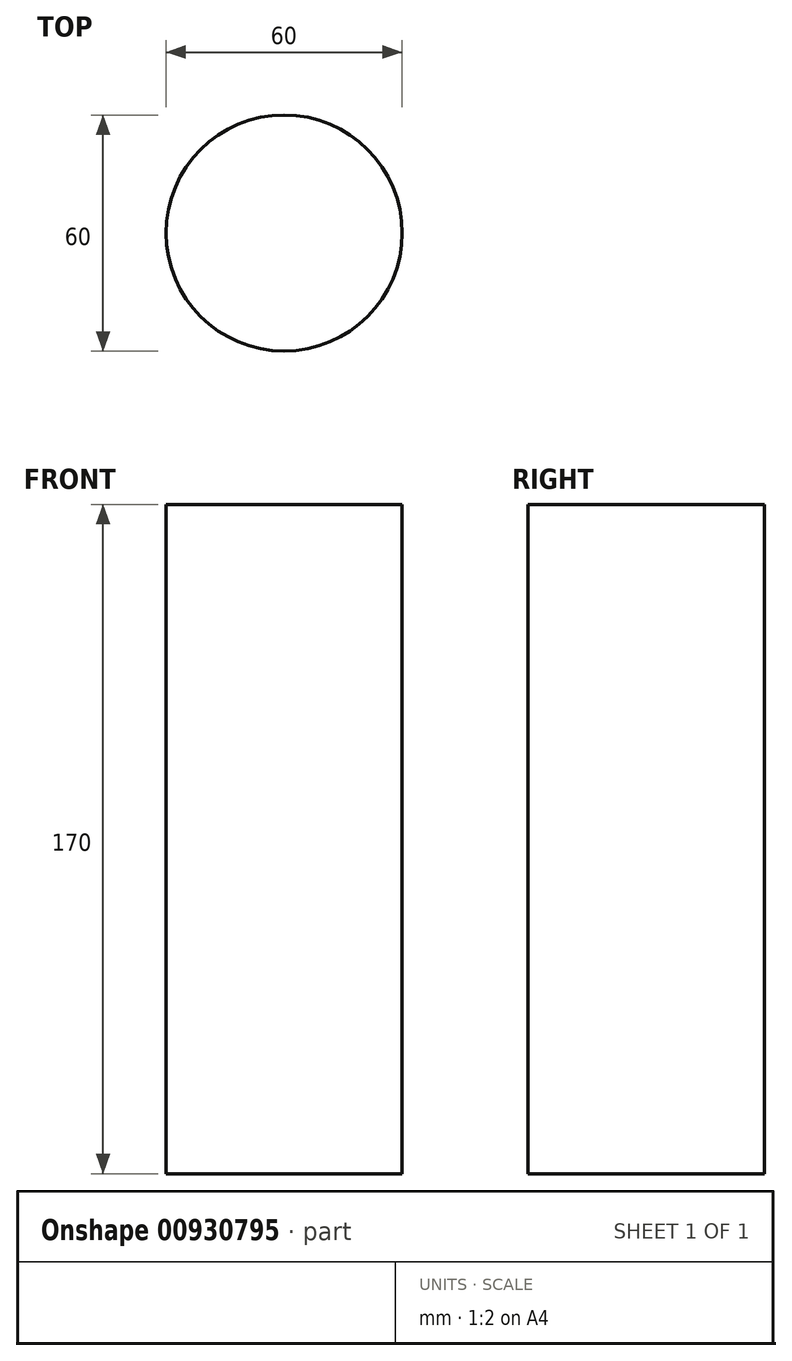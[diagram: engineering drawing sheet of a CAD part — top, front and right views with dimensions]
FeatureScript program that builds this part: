
annotation { "Feature Type Name" : "Feature", "Feature Type Description" : "" }
export const myFeature = defineFeature(function(context is Context, id is Id, definition is map)
    precondition{}
    {
        {
            var Q0;
            Q0=qCreatedBy(makeId("Top.planeOp"),FACE);
            var sketch = newSketch(context, id + "F0", { "sketchPlane" : qUnion([Q0])});
            skLineSegment(sketch, "E0.bottom", {"start": v(0, 0) * mm, "end": v(-30, 0) * mm});
            skLineSegment(sketch, "E0.top", {"start": v(0, 30) * mm, "end": v(-30, 30) * mm});
            skLineSegment(sketch, "E0.left", {"start": v(0, 0) * mm, "end": v(0, 30) * mm});
            skLineSegment(sketch, "E0.right", {"start": v(-30, 0) * mm, "end": v(-30, 30) * mm});
            skSolve(sketch);
        }
        {
            var Q0;
            Q0 = qSketchRegion(id + "F0", true);
            extrude(context, id + "F1", {"entities" : qUnion([Q0]), "depth" : 30 * mm, "offsetDistance" : 25 * mm});
        }
        {
            var Q0;
            Q0=makeQuery(id+"F1.opExtrude","SWEPT_FACE",FACE,{"disambiguationData":[OSD([sQuery(id+"F0.wireOp",EDGE,"E0.right")])]});
            var sketch = newSketch(context, id + "F2", { "sketchPlane" : qUnion([Q0])});
            skLineSegment(sketch, "E1", {"start": v(0, 0) * mm, "end": v(-30, 30) * mm});
            skLineSegment(sketch, "E2", {"start": v(0, 30) * mm, "end": v(-30, 0) * mm});
            skCircle(sketch, "E3", {"center": v(-15, 15) * mm, "radius": 10 * mm});
            skSolve(sketch);
        }
        {
            var Q0;
            Q0 = qSketchRegion(id + "F2", true);
            extrude(context, id + "F3", {"entities" : qUnion([Q0]), "operationType" : NewBodyOperationType.REMOVE, "oppositeDirection" : true, "depth" : 15 * mm, "offsetDistance" : 25 * mm});
        }
        {
            var Q0;
            Q0=makeQuery(id+"F1.opExtrude","CAP_EDGE",EDGE,{"disambiguationData":[OSD([sQuery(id+"F0.wireOp",EDGE,"E0.top")])],"isStart":false});
            var Q1;
            Q1=makeQuery(id+"F1.opExtrude","CAP_EDGE",EDGE,{"disambiguationData":[OSD([sQuery(id+"F0.wireOp",EDGE,"E0.top")])],"isStart":true});
            var Q2;
            Q2=makeQuery(id+"F1.opExtrude","CAP_EDGE",EDGE,{"disambiguationData":[OSD([sQuery(id+"F0.wireOp",EDGE,"E0.bottom")])],"isStart":true});
            var Q3;
            Q3=makeQuery(id+"F1.opExtrude","CAP_EDGE",EDGE,{"disambiguationData":[OSD([sQuery(id+"F0.wireOp",EDGE,"E0.bottom")])],"isStart":false});
            var Q4;
            Q4=makeQuery(id+"F1.opExtrude","SWEPT_EDGE",EDGE,{"disambiguationData":[OSD([sQuery(id+"F0.wireOp",EDGE,"E0.bottom"),sQuery(id+"F0.wireOp",EDGE,"E0.right")])]});
            var Q5;
            Q5=makeQuery(id+"F1.opExtrude","CAP_EDGE",EDGE,{"disambiguationData":[OSD([sQuery(id+"F0.wireOp",EDGE,"E0.right")])],"isStart":true});
            var Q6;
            Q6=makeQuery(id+"F1.opExtrude","SWEPT_EDGE",EDGE,{"disambiguationData":[OSD([sQuery(id+"F0.wireOp",EDGE,"E0.top"),sQuery(id+"F0.wireOp",EDGE,"E0.right")])]});
            var Q7;
            Q7=makeQuery(id+"F1.opExtrude","CAP_EDGE",EDGE,{"disambiguationData":[OSD([sQuery(id+"F0.wireOp",EDGE,"E0.right")])],"isStart":false});
            fillet(context, id + "F4", {"entities" : qUnion([Q0, Q1, Q2, Q3, Q4, Q5, Q6, Q7]), "radius" : 6 * mm, "tangentPropagation" : true, "allowEdgeOverflow" : false});
        }
        {
            var Q0;
            Q0=makeQuery(id+"F1.opExtrude","SWEPT_FACE",FACE,{"disambiguationData":[OSD([sQuery(id+"F0.wireOp",EDGE,"E0.bottom")])]});
            var sketch = newSketch(context, id + "F5", { "sketchPlane" : qUnion([Q0])});
            skText(sketch, "E4", { "text": "DV", "fontName": "OpenSans-Regular.ttf"});
            const initialGuessF5  = {"E4": [-0.0229, 0.01065, 1, 0, 0.00881]};
            skSetInitialGuess(sketch, initialGuessF5);
            skSolve(sketch);
        }
        {
            var Q0;
            Q0 = qSketchRegion(id + "F5", true);
            extrude(context, id + "F6", {"entities" : qUnion([Q0]), "operationType" : NewBodyOperationType.ADD, "depth" : 2 * mm, "offsetDistance" : 25 * mm});
        }
        {
            var Q0;
            Q0=qCreatedBy(makeId("Right.planeOp"),FACE);
            var sketch = newSketch(context, id + "F7", { "sketchPlane" : qUnion([Q0])});
            skLineSegment(sketch, "E5.bottom", {"start": v(-11.13, -10.55) * mm, "end": v(44.54, -10.55) * mm});
            skLineSegment(sketch, "E5.top", {"start": v(-11.13, 40.87) * mm, "end": v(44.54, 40.87) * mm});
            skLineSegment(sketch, "E5.left", {"start": v(-11.13, -10.55) * mm, "end": v(-11.13, 40.87) * mm});
            skLineSegment(sketch, "E5.right", {"start": v(44.54, -10.55) * mm, "end": v(44.54, 40.87) * mm});
            skSolve(sketch);
        }
        {
            var Q0;
            Q0 = qSketchRegion(id + "F7", true);
            extrude(context, id + "F8", {"entities" : qUnion([Q0]), "oppositeDirection" : true, "depth" : 50 * mm, "offsetDistance" : 25 * mm});
        }
        {
            var Q0;
            Q0=makeQuery(id+"F1.opExtrude","SWEPT_BODY",BODY,{"disambiguationData":[OSD([sQuery(id+"F0.wireOp",EDGE,"E0.bottom"),sQuery(id+"F0.wireOp",EDGE,"E0.top"),sQuery(id+"F0.wireOp",EDGE,"E0.left"),sQuery(id+"F0.wireOp",EDGE,"E0.right")])]});
            var Q1;
            Q1=makeQuery(id+"F8.opExtrude","SWEPT_BODY",BODY,{"disambiguationData":[OSD([sQuery(id+"F7.wireOp",EDGE,"E5.bottom"),sQuery(id+"F7.wireOp",EDGE,"E5.top"),sQuery(id+"F7.wireOp",EDGE,"E5.left"),sQuery(id+"F7.wireOp",EDGE,"E5.right")])]});
            booleanBodies(context, id + "F9", {"operationType" : BooleanOperationType.SUBTRACTION, "tools" : qUnion([Q0]), "targets" : qUnion([Q1]), "offset" : true, "offsetAll" : true, "offsetDistance" : 4 * mm});
        }
        {
            var Q0;
            Q0=makeQuery(id+"F8.opExtrude","SWEPT_BODY",BODY,{"disambiguationData":[OSD([sQuery(id+"F7.wireOp",EDGE,"E5.bottom"),sQuery(id+"F7.wireOp",EDGE,"E5.top"),sQuery(id+"F7.wireOp",EDGE,"E5.left"),sQuery(id+"F7.wireOp",EDGE,"E5.right")])]});
            deleteBodies(context, id + "F10", {"entities" : qUnion([Q0])});
        }
        {
            var Q0;
            Q0=qCreatedBy(makeId("Top.planeOp"),FACE);
            var sketch = newSketch(context, id + "F11", { "sketchPlane" : qUnion([Q0])});
            skCircle(sketch, "E6", {"center": v(0, 0) * mm, "radius": 30 * mm});
            skSolve(sketch);
        }
        {
            var Q0;
            Q0 = qSketchRegion(id + "F11", true);
            extrude(context, id + "F12", {"entities" : qUnion([Q0]), "depth" : 170 * mm, "offsetDistance" : 25 * mm});
        }
    });
